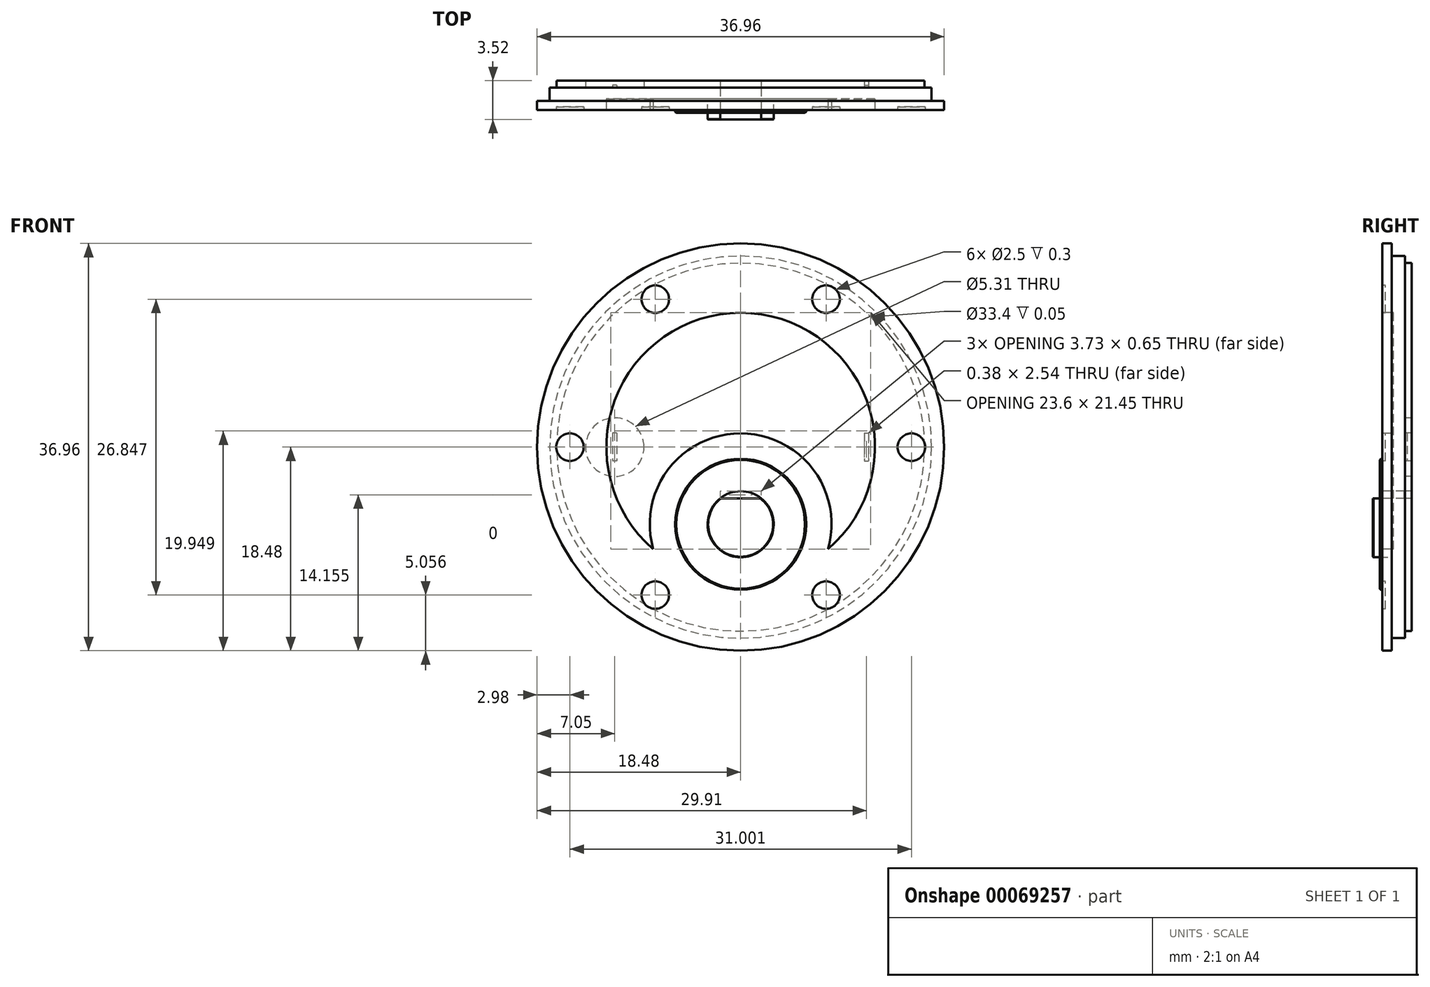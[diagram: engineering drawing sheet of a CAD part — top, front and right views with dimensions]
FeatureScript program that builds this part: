
annotation { "Feature Type Name" : "Feature", "Feature Type Description" : "" }
export const myFeature = defineFeature(function(context is Context, id is Id, definition is map)
    precondition{}
    {
        {
            assignVariable(context, id + "F0", {"name" : "body_length", "anyValue" : 1.21});
        }
        {
            var Q0;
            Q0=qCreatedBy(makeId("Front.planeOp"),FACE);
            var sketch = newSketch(context, id + "F1", { "sketchPlane" : qUnion([Q0])});
            skCircle(sketch, "E0", {"center": v(0, 0) * mm, "radius": 17.34 * mm});
            skSolve(sketch);
        }
        {
            var Q0;
            Q0=makeQuery(id+"F1.imprint","IMPRINT",FACE,{"disambiguationData":[TD([[makeQuery(id+"F1.imprint","IMPRINT",EDGE,{"derivedFrom":sQuery(id+"F1.wireOp",EDGE,"E0")}),1.0]])]});
            extrude(context, id + "F2", {"entities" : qUnion([Q0]), "oppositeDirection" : true, "depth" : (getVariable(context, 'body_length')) * mm});
        }
        {
            assignVariable(context, id + "F3", {"name" : "shell_relief", "anyValue" : 0.05});
        }
        {
            var Q0;
            Q0=makeQuery(id+"F2.opExtrude","CAP_FACE",FACE,{"disambiguationData":[OSD([sQuery(id+"F1.wireOp",EDGE,"E0")])],"isStart":false});
            var sketch = newSketch(context, id + "F4", { "sketchPlane" : qUnion([Q0])});
            skCircle(sketch, "E1.0", {"center": v(0, 0) * mm, "radius": 17.34 * mm});
            skCircle(sketch, "E2", {"center": v(0, 0) * mm, "radius": 16.7 * mm});
            skSolve(sketch);
        }
        {
            var Q0;
            Q0=makeQuery(id+"F4.imprint","IMPRINT",FACE,{"disambiguationData":[TD([[makeQuery(id+"F4.imprint","IMPRINT",EDGE,{"derivedFrom":sQuery(id+"F4.wireOp",EDGE,"E2")}),1.0]])]});
            extrude(context, id + "F5", {"entities" : qUnion([Q0]), "operationType" : NewBodyOperationType.REMOVE, "oppositeDirection" : true, "depth" : (getVariable(context, 'shell_relief')) * mm});
        }
        {
            assignVariable(context, id + "F6", {"name" : "gearbox_length", "anyValue" : 0.84});
        }
        {
            var Q0;
            Q0=qCreatedBy(makeId("Front.planeOp"),FACE);
            var sketch = newSketch(context, id + "F7", { "sketchPlane" : qUnion([Q0])});
            skCircle(sketch, "E3", {"center": v(0, 0) * mm, "radius": 18.48 * mm});
            skSolve(sketch);
        }
        {
            var Q0;
            Q0=makeQuery(id+"F7.imprint","IMPRINT",FACE,{"disambiguationData":[TD([[makeQuery(id+"F7.imprint","IMPRINT",EDGE,{"derivedFrom":sQuery(id+"F7.wireOp",EDGE,"E3")}),1.0]])]});
            extrude(context, id + "F8", {"entities" : qUnion([Q0]), "depth" : (getVariable(context, 'gearbox_length')) * mm});
        }
        {
            assignVariable(context, id + "F9", {"name" : "shoulder_length", "anyValue" : 0.23});
        }
        {
            var Q0;
            Q0=makeQuery(id+"F8.opExtrude","CAP_FACE",FACE,{"disambiguationData":[OSD([sQuery(id+"F7.wireOp",EDGE,"E3")])],"isStart":false});
            var sketch = newSketch(context, id + "F10", { "sketchPlane" : qUnion([Q0])});
            skPoint(sketch, "E4.0", {"position": v(0, 0) * mm});
            skCircle(sketch, "E5", {"center": v(0, -7) * mm, "radius": 5.94 * mm});
            skSolve(sketch);
        }
        {
            var Q0;
            Q0=makeQuery(id+"F10.imprint","IMPRINT",FACE,{"disambiguationData":[TD([[makeQuery(id+"F10.imprint","IMPRINT",EDGE,{"derivedFrom":sQuery(id+"F10.wireOp",EDGE,"E5")}),1.0]])]});
            extrude(context, id + "F11", {"entities" : qUnion([Q0]), "operationType" : NewBodyOperationType.ADD, "depth" : (getVariable(context, 'shoulder_length')) * mm});
        }
        {
            assignVariable(context, id + "F12", {"name" : "screw_hole_depth", "anyValue" : 0.3});
        }
        {
            var Q0;
            Q0=makeQuery(id+"F8.opExtrude","CAP_FACE",FACE,{"disambiguationData":[OSD([sQuery(id+"F7.wireOp",EDGE,"E3")])],"isStart":false});
            var sketch = newSketch(context, id + "F13", { "sketchPlane" : qUnion([Q0])});
            skCircle(sketch, "E6", {"center": v(0, 0) * mm, "radius": 15.5 * mm, "construction": true});
            skCircle(sketch, "E7", {"center": v(-15.5, 0) * mm, "radius": 1.25 * mm});
            skCircle(sketch, "E8.1.0", {"center": v(-7.75, -13.42) * mm, "radius": 1.25 * mm});
            skCircle(sketch, "E8.2.0", {"center": v(7.75, -13.42) * mm, "radius": 1.25 * mm});
            skCircle(sketch, "E8.3.0", {"center": v(15.5, 0) * mm, "radius": 1.25 * mm});
            skCircle(sketch, "E8.4.0", {"center": v(7.75, 13.42) * mm, "radius": 1.25 * mm});
            skCircle(sketch, "E8.5.0", {"center": v(-7.75, 13.42) * mm, "radius": 1.25 * mm});
            skSolve(sketch);
        }
        {
            var Q0;
            Q0 = qSketchRegion(id + "F13", true);
            extrude(context, id + "F14", {"entities" : qUnion([Q0]), "operationType" : NewBodyOperationType.REMOVE, "oppositeDirection" : true, "depth" : (getVariable(context, 'screw_hole_depth')) * mm});
        }
        {
            var Q0;
            Q0=makeQuery(id+"F8.opExtrude","CAP_FACE",FACE,{"disambiguationData":[OSD([sQuery(id+"F7.wireOp",EDGE,"E3")])],"isStart":false});
            var sketch = newSketch(context, id + "F15", { "sketchPlane" : qUnion([Q0])});
            skCircle(sketch, "E9", {"center": v(0, 0) * mm, "radius": 12.2 * mm});
            skCircle(sketch, "E10.0", {"center": v(0, -7) * mm, "radius": 5.94 * mm});
            skCircle(sketch, "E11", {"center": v(0, -7) * mm, "radius": 8.25 * mm});
            skSolve(sketch);
        }
        {
            var Q0;
            {var subQ0=sQuery(id+"F15.wireOp",EDGE,"E11");var subQ1=sQuery(id+"F15.wireOp",EDGE,"E9");var subQ2=makeQuery(id+"F15.imprint","INTERSECT",VERTEX,{"disambiguationData":[OD(0.0)],"derivedFrom":[subQ1,subQ0]});Q0=makeQuery(id+"F15.imprint","IMPRINT",FACE,{"disambiguationData":[TD([[makeQuery(id+"F15.imprint","IMPRINT",EDGE,{"disambiguationData":[TD([[subQ2,1.0]])],"derivedFrom":subQ1}),1.0]])]});}
            extrude(context, id + "F16", {"entities" : qUnion([Q0]), "operationType" : NewBodyOperationType.REMOVE, "oppositeDirection" : true, "depth" : 1.02 * mm});
        }
        {
            assignVariable(context, id + "F17", {"name" : "shaft_length", "anyValue" : 0.62});
        }
        {
            var Q0;
            Q0=makeQuery(id+"F11.opExtrude","CAP_FACE",FACE,{"disambiguationData":[OSD([sQuery(id+"F10.wireOp",EDGE,"E5")])],"isStart":false});
            var sketch = newSketch(context, id + "F18", { "sketchPlane" : qUnion([Q0])});
            skCircle(sketch, "E12.0", {"center": v(0, -7) * mm, "radius": 5.94 * mm});
            skCircle(sketch, "E13", {"center": v(0, -7) * mm, "radius": 3 * mm});
            skSolve(sketch);
        }
        {
            var Q0;
            Q0=makeQuery(id+"F18.imprint","IMPRINT",FACE,{"disambiguationData":[TD([[makeQuery(id+"F18.imprint","IMPRINT",EDGE,{"derivedFrom":sQuery(id+"F18.wireOp",EDGE,"E13")}),1.0]])]});
            var Q1;
            Q1=makeQuery(id+"F2.opExtrude","SWEPT_BODY",BODY,{"disambiguationData":[OSD([sQuery(id+"F1.wireOp",EDGE,"E0")])]});
            extrude(context, id + "F19", {"entities" : qUnion([Q0]), "depth" : (getVariable(context, 'shaft_length')) * mm, "hasSecondDirection" : true, "secondDirectionBound" : BoundingType.UP_TO_BODY, "secondDirectionOppositeDirection" : true, "secondDirectionBoundEntityBody" : qUnion([Q1]), "secondDirectionDepth" : 25.4 * mm});
        }
        {
            assignVariable(context, id + "F20", {"name" : "flat_length", "anyValue" : 12 * mm});
        }
        {
            var Q0;
            Q0=makeQuery(id+"F19.opExtrude","CAP_FACE",FACE,{"disambiguationData":[OSD([sQuery(id+"F18.wireOp",EDGE,"E13")])],"isStart":false});
            var sketch = newSketch(context, id + "F21", { "sketchPlane" : qUnion([Q0])});
            skLineSegment(sketch, "E14", {"start": v(-1.86, -4.65) * mm, "end": v(1.86, -4.65) * mm});
            skPoint(sketch, "E15", {"position": v(0, -10) * mm});
            skSolve(sketch);
        }
        {
            var Q0;
            {var subQ0=sQuery(id+"F21.wireOp",EDGE,"E14");Q0=makeQuery(id+"F21.imprint","IMPRINT",FACE,{"disambiguationData":[TD([[makeQuery(id+"F21.imprint","IMPRINT",EDGE,{"derivedFrom":subQ0}),1.0]])]});}
            extrude(context, id + "F22", {"entities" : qUnion([Q0]), "operationType" : NewBodyOperationType.REMOVE, "oppositeDirection" : true, "depth" : getVariable(context, 'flat_length')});
        }
        {
            assignVariable(context, id + "F23", {"name" : "shoulder_chamfer", "anyValue" : .1});
        }
        {
            var Q0;
            Q0=makeQuery(id+"F11.opExtrude","CAP_EDGE",EDGE,{"disambiguationData":[OSD([sQuery(id+"F10.wireOp",EDGE,"E5")])],"isStart":false});
            chamfer(context, id + "F24", {"entities" : qUnion([Q0]), "width" : (getVariable(context, 'shoulder_chamfer')) * mm, "tangentPropagation" : true});
        }
        {
            assignVariable(context, id + "F25", {"name" : "shaft_chamfer", "anyValue" : getVariable(context, 'shoulder_chamfer') / 2});
        }
        {
            var Q0;
            Q0=makeQuery(id+"F19.opExtrude","CAP_EDGE",EDGE,{"disambiguationData":[OSD([sQuery(id+"F18.wireOp",EDGE,"E13")])],"isStart":false});
            chamfer(context, id + "F26", {"entities" : qUnion([Q0]), "width" : (getVariable(context, 'shaft_chamfer')) * mm, "tangentPropagation" : true});
        }
        {
            assignVariable(context, id + "F27", {"name" : "tab_height", "anyValue" : 0.25});
        }
        {
            assignVariable(context, id + "F28", {"name" : "tab_shoulder_height", "anyValue" : .67});
        }
        {
            var Q0;
            Q0=makeQuery(id+"F5.boolean.opBoolean","COPY",FACE,{"derivedFrom":makeQuery(id+"F5.opExtrude","CAP_FACE",FACE,{"disambiguationData":[OSD([sQuery(id+"F4.wireOp",EDGE,"E2")])],"isStart":false})});
            var sketch = newSketch(context, id + "F29", { "sketchPlane" : qUnion([Q0])});
            skPoint(sketch, "E16.0", {"position": v(0, 0) * mm});
            skCircle(sketch, "E17", {"center": v(-11.43, 0) * mm, "radius": 2.65 * mm});
            skCircle(sketch, "E18.MirrorC", {"center": v(11.43, 0) * mm, "radius": 2.65 * mm});
            skLineSegment(sketch, "E19.rect.bottom", {"start": v(-11.24, 1.27) * mm, "end": v(-11.62, 1.27) * mm});
            skLineSegment(sketch, "E19.rect.top", {"start": v(-11.24, -1.27) * mm, "end": v(-11.62, -1.27) * mm});
            skLineSegment(sketch, "E19.rect.left", {"start": v(-11.24, 1.27) * mm, "end": v(-11.24, -1.27) * mm});
            skLineSegment(sketch, "E19.rect.right", {"start": v(-11.62, 1.27) * mm, "end": v(-11.62, -1.27) * mm});
            skLineSegment(sketch, "E20.MirrorCS", {"start": v(11.24, -1.27) * mm, "end": v(11.62, -1.27) * mm});
            skLineSegment(sketch, "E21.MirrorCS", {"start": v(11.24, 1.27) * mm, "end": v(11.62, 1.27) * mm});
            skLineSegment(sketch, "E22.MirrorCS", {"start": v(11.24, 1.27) * mm, "end": v(11.24, -1.27) * mm});
            skLineSegment(sketch, "E23.MirrorCS", {"start": v(11.62, 1.27) * mm, "end": v(11.62, -1.27) * mm});
            skSolve(sketch);
        }
        {
            var Q0;
            Q0=makeQuery(id+"F29.imprint","IMPRINT",FACE,{"disambiguationData":[TD([[makeQuery(id+"F29.imprint","IMPRINT",EDGE,{"derivedFrom":sQuery(id+"F29.wireOp",EDGE,"E17")}),1.0]])]});
            var Q1;
            Q1=makeQuery(id+"F29.imprint","IMPRINT",FACE,{"disambiguationData":[TD([[makeQuery(id+"F29.imprint","IMPRINT",EDGE,{"derivedFrom":sQuery(id+"F29.wireOp",EDGE,"E18.MirrorC")}),-1.0]])]});
            extrude(context, id + "F30", {"entities" : qUnion([Q0, Q1]), "depth" : (getVariable(context, 'tab_shoulder_height')) * mm});
        }
        {
            var Q0;
            Q0=makeQuery(id+"F29.imprint","IMPRINT",FACE,{"disambiguationData":[TD([[makeQuery(id+"F29.imprint","IMPRINT",EDGE,{"derivedFrom":sQuery(id+"F29.wireOp",EDGE,"E19.rect.bottom")}),1.0]])]});
            var Q1;
            Q1=makeQuery(id+"F29.imprint","IMPRINT",FACE,{"disambiguationData":[TD([[makeQuery(id+"F29.imprint","IMPRINT",EDGE,{"derivedFrom":sQuery(id+"F29.wireOp",EDGE,"E20.MirrorCS")}),1.0]])]});
            extrude(context, id + "F31", {"entities" : qUnion([Q0, Q1]), "depth" : (getVariable(context, 'tab_height')) * mm});
        }
    });
